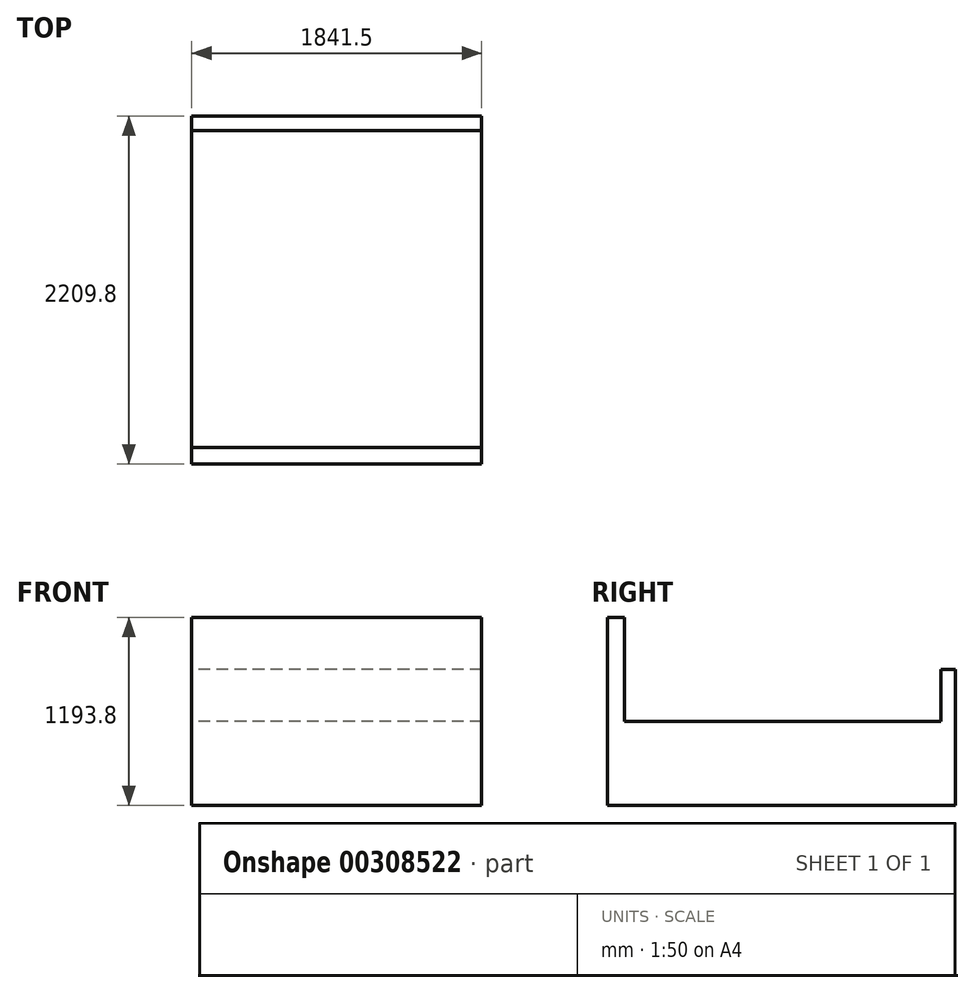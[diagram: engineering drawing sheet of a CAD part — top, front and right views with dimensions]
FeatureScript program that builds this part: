
annotation { "Feature Type Name" : "Feature", "Feature Type Description" : "" }
export const myFeature = defineFeature(function(context is Context, id is Id, definition is map)
    precondition{}
    {
        {
            var Q0;
            Q0=qCreatedBy(makeId("Front.planeOp"),FACE);
            var sketch = newSketch(context, id + "F0", { "sketchPlane" : qUnion([Q0])});
            skLineSegment(sketch, "E0.bottom", {"start": v(920.75, -266.7) * mm, "end": v(-920.75, -266.7) * mm});
            skLineSegment(sketch, "E0.top", {"start": v(920.75, 266.7) * mm, "end": v(-920.75, 266.7) * mm});
            skLineSegment(sketch, "E0.left", {"start": v(920.75, -266.7) * mm, "end": v(920.75, 266.7) * mm});
            skLineSegment(sketch, "E0.right", {"start": v(-920.75, -266.7) * mm, "end": v(-920.75, 266.7) * mm});
            skPoint(sketch, "E0.middle", {"position": v(0, 0) * mm});
            skSolve(sketch);
        }
        {
            var Q0;
            Q0=makeQuery(id+"F0.imprint","IMPRINT",FACE,{"disambiguationData":[TD([[makeQuery(id+"F0.imprint","IMPRINT",EDGE,{"derivedFrom":sQuery(id+"F0.wireOp",EDGE,"E0.bottom")}),-1.0]])]});
            extrude(context, id + "F1", {"entities" : qUnion([Q0]), "depth" : 2209.8 * mm});
        }
        {
            var Q0;
            Q0=makeQuery(id+"F1.opExtrude","SWEPT_FACE",FACE,{"disambiguationData":[OSD([sQuery(id+"F0.wireOp",EDGE,"E0.top")])]});
            var sketch = newSketch(context, id + "F2", { "sketchPlane" : qUnion([Q0])});
            skLineSegment(sketch, "E1.bottom", {"start": v(-920.75, -2209.8) * mm, "end": v(920.75, -2209.8) * mm});
            skLineSegment(sketch, "E1.top", {"start": v(-920.75, -2103.97) * mm, "end": v(920.75, -2103.97) * mm});
            skLineSegment(sketch, "E1.left", {"start": v(-920.75, -2209.8) * mm, "end": v(-920.75, -2103.97) * mm});
            skLineSegment(sketch, "E1.right", {"start": v(920.75, -2209.8) * mm, "end": v(920.75, -2103.97) * mm});
            skSolve(sketch);
        }
        {
            var Q0;
            Q0 = qSketchRegion(id + "F2", true);
            extrude(context, id + "F3", {"entities" : qUnion([Q0]), "operationType" : NewBodyOperationType.ADD, "depth" : 660.4 * mm});
        }
        {
            var Q0;
            Q0=makeQuery(id+"F1.opExtrude","SWEPT_FACE",FACE,{"disambiguationData":[OSD([sQuery(id+"F0.wireOp",EDGE,"E0.top")])]});
            var sketch = newSketch(context, id + "F4", { "sketchPlane" : qUnion([Q0])});
            skLineSegment(sketch, "E2.bottom", {"start": v(920.75, 0) * mm, "end": v(-920.75, 0) * mm});
            skLineSegment(sketch, "E2.top", {"start": v(920.75, -92.77) * mm, "end": v(-920.75, -92.77) * mm});
            skLineSegment(sketch, "E2.left", {"start": v(920.75, 0) * mm, "end": v(920.75, -92.77) * mm});
            skLineSegment(sketch, "E2.right", {"start": v(-920.75, 0) * mm, "end": v(-920.75, -92.77) * mm});
            skSolve(sketch);
        }
        {
            var Q0;
            Q0=makeQuery(id+"F4.imprint","IMPRINT",FACE,{"disambiguationData":[TD([[makeQuery(id+"F4.imprint","IMPRINT",EDGE,{"derivedFrom":sQuery(id+"F4.wireOp",EDGE,"E2.bottom")}),1.0]])]});
            extrude(context, id + "F5", {"entities" : qUnion([Q0]), "operationType" : NewBodyOperationType.ADD, "depth" : 330.2 * mm});
        }
    });
